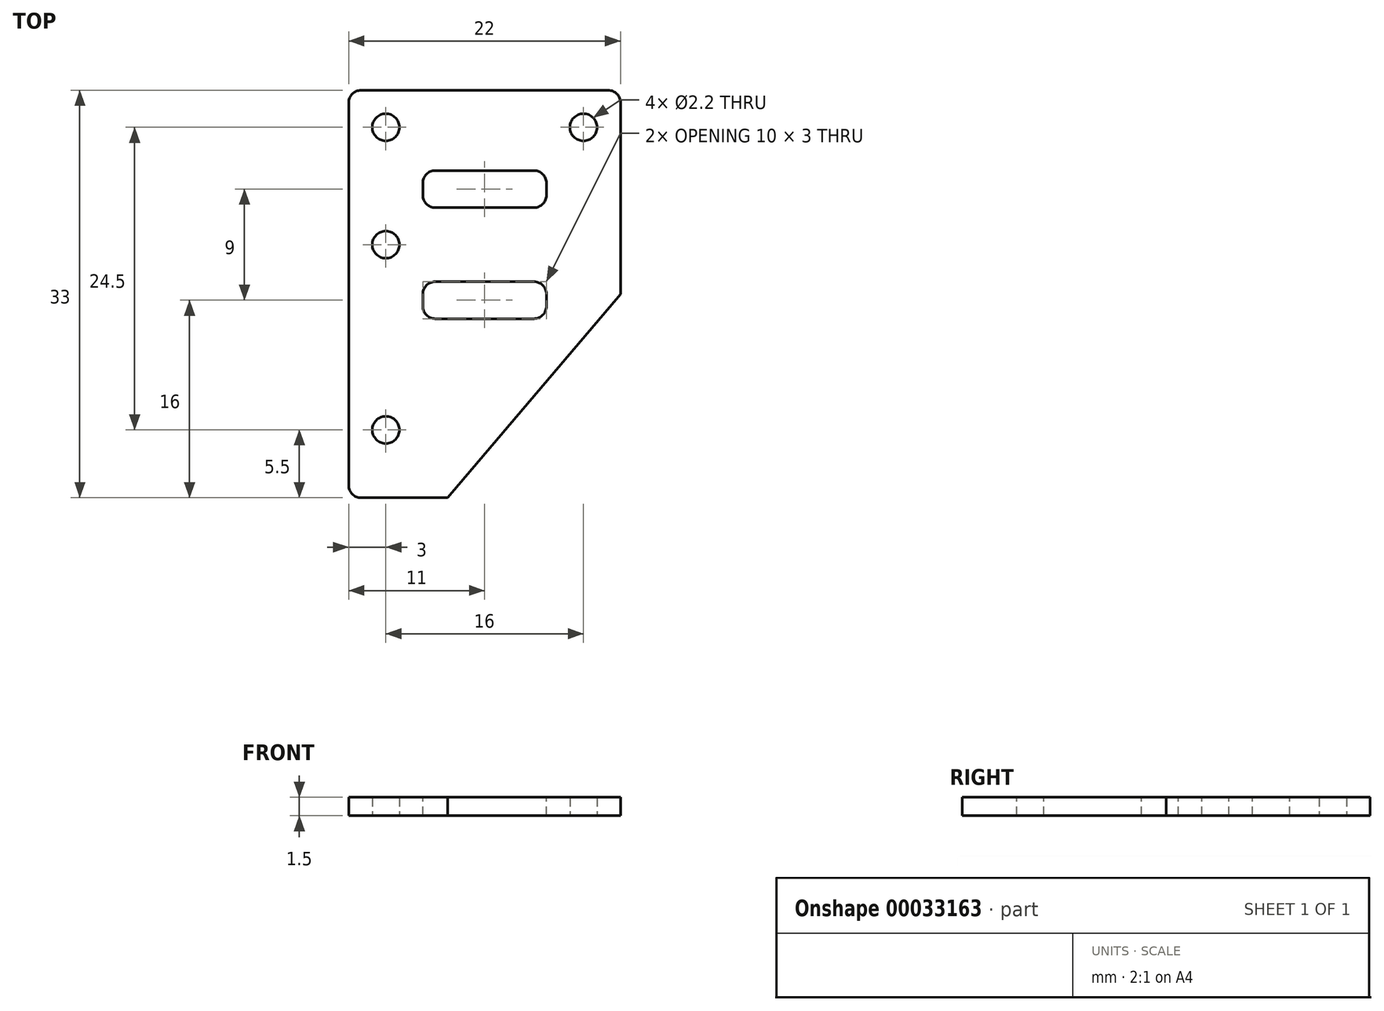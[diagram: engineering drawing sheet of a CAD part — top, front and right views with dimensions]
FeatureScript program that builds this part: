
annotation { "Feature Type Name" : "Feature", "Feature Type Description" : "" }
export const myFeature = defineFeature(function(context is Context, id is Id, definition is map)
    precondition{}
    {
        {
            var Q0;
            Q0=qCreatedBy(makeId("Top.planeOp"),FACE);
            var sketch = newSketch(context, id + "F0", { "sketchPlane" : qUnion([Q0])});
            skLineSegment(sketch, "E0.bottom", {"start": v(11, 16.5) * mm, "end": v(-11, 16.5) * mm});
            skLineSegment(sketch, "E0.top", {"start": v(11, -16.5) * mm, "end": v(-11, -16.5) * mm});
            skLineSegment(sketch, "E0.left", {"start": v(11, 16.5) * mm, "end": v(11, -16.5) * mm});
            skLineSegment(sketch, "E0.right", {"start": v(-11, 16.5) * mm, "end": v(-11, -16.5) * mm});
            skPoint(sketch, "E0.middle", {"position": v(0, 0) * mm});
            skCircle(sketch, "E1", {"center": v(8, 13.5) * mm, "radius": 1.1 * mm});
            skCircle(sketch, "E2.MirrorC", {"center": v(-8, 13.5) * mm, "radius": 1.1 * mm});
            skSolve(sketch);
        }
        {
            var Q0;
            {var subQ4=sQuery(id+"F0.wireOp",EDGE,"E0.bottom");Q0=makeQuery(id+"F0.imprint","IMPRINT",FACE,{"disambiguationData":[TD([[makeQuery(id+"F0.imprint","IMPRINT",EDGE,{"derivedFrom":subQ4}),1.0]])]});}
            var Q1;
            {var subQ2=sQuery(id+"F0.wireOp",EDGE,"f1e16323-2be2-4770-a9bf-99cfb16d4013.1.0.0");Q1=makeQuery(id+"F0.imprint","IMPRINT",FACE,{"disambiguationData":[TD([[makeQuery(id+"F0.imprint","IMPRINT",EDGE,{"derivedFrom":subQ2}),-1.0]])]});}
            extrude(context, id + "F1", {"entities" : qUnion([Q0, Q1]), "depth" : 1.5 * mm});
        }
        {
            var Q0;
            Q0=makeQuery(id+"F1.opExtrude","CAP_FACE",FACE,{"disambiguationData":[OSD([sQuery(id+"F0.wireOp",EDGE,"E0.bottom"),sQuery(id+"F0.wireOp",EDGE,"E0.top"),sQuery(id+"F0.wireOp",EDGE,"E0.left"),sQuery(id+"F0.wireOp",EDGE,"E0.right"),sQuery(id+"F0.wireOp",EDGE,"E1"),sQuery(id+"F0.wireOp",EDGE,"E2.MirrorC"),sQuery(id+"F0.wireOp",EDGE,"1bDBTO5W-hAAF-Dv1a-i1w2-BnnXARTyQX5s"),sQuery(id+"F0.wireOp",EDGE,"f1e16323-2be2-4770-a9bf-99cfb16d4013.1.0.0"),sQuery(id+"F0.wireOp",EDGE,"jiPMqsls-zV3J-hMdb-mDSb-S4SgiakzvMcZ")])],"isStart":false});
            var sketch = newSketch(context, id + "F2", { "sketchPlane" : qUnion([Q0])});
            skLineSegment(sketch, "E3", {"start": v(0, 16.5) * mm, "end": v(0, -16.5) * mm, "construction": true});
            skLineSegment(sketch, "E4.bottom", {"start": v(-4, 10) * mm, "end": v(4, 10) * mm});
            skLineSegment(sketch, "E4.top", {"start": v(-4, 7) * mm, "end": v(4, 7) * mm});
            skLineSegment(sketch, "E4.left", {"start": v(-5, 9) * mm, "end": v(-5, 8) * mm});
            skLineSegment(sketch, "E4.right", {"start": v(5, 9) * mm, "end": v(5, 8) * mm});
            skPoint(sketch, "E4.middle", {"position": v(0, 8.5) * mm});
            skPoint(sketch, "E5", {"position": v(-8, 13.5) * mm});
            skPoint(sketch, "E6.visualSharp", {"position": v(-5, 10) * mm});
            skArc(sketch, "E6.filletArc", {"start": v(-4, 10) * mm, "mid": v(-4.7, 9.7) * mm, "end": v(-5, 9) * mm});
            skPoint(sketch, "E7.visualSharp", {"position": v(-5, 7) * mm});
            skArc(sketch, "E7.filletArc", {"start": v(-5, 8) * mm, "mid": v(-4.7, 7.3) * mm, "end": v(-4, 7) * mm});
            skPoint(sketch, "E8.visualSharp", {"position": v(5, 10) * mm});
            skArc(sketch, "E8.filletArc", {"start": v(5, 9) * mm, "mid": v(4.7, 9.7) * mm, "end": v(4, 10) * mm});
            skPoint(sketch, "E9.visualSharp", {"position": v(5, 7) * mm});
            skArc(sketch, "E9.filletArc", {"start": v(4, 7) * mm, "mid": v(4.7, 7.3) * mm, "end": v(5, 8) * mm});
            skPoint(sketch, "E10.1.0.0", {"position": v(5, 1) * mm});
            skPoint(sketch, "E10.1.0.1", {"position": v(0, -0.5) * mm});
            skPoint(sketch, "E10.1.0.2", {"position": v(-5, 1) * mm});
            skPoint(sketch, "E10.1.0.3", {"position": v(-5, -2) * mm});
            skPoint(sketch, "E10.1.0.4", {"position": v(5, -2) * mm});
            skLineSegment(sketch, "E10.1.0.5", {"start": v(-4, 1) * mm, "end": v(4, 1) * mm});
            skLineSegment(sketch, "E10.1.0.6", {"start": v(-4, -2) * mm, "end": v(4, -2) * mm});
            skArc(sketch, "E10.1.0.7", {"start": v(4, -2) * mm, "mid": v(4.7, -1.7) * mm, "end": v(5, -1) * mm});
            skArc(sketch, "E10.1.0.8", {"start": v(5, 0) * mm, "mid": v(4.7, 0.7) * mm, "end": v(4, 1) * mm});
            skArc(sketch, "E10.1.0.9", {"start": v(-5, -1) * mm, "mid": v(-4.7, -1.7) * mm, "end": v(-4, -2) * mm});
            skLineSegment(sketch, "E10.1.0.10", {"start": v(-5, 0) * mm, "end": v(-5, -1) * mm});
            skLineSegment(sketch, "E10.1.0.11", {"start": v(5, 0) * mm, "end": v(5, -1) * mm});
            skArc(sketch, "E10.1.0.12", {"start": v(-4, 1) * mm, "mid": v(-4.7, 0.7) * mm, "end": v(-5, 0) * mm});
            skLineSegment(sketch, "E10.direction1", {"start": v(-5, 7) * mm, "end": v(-5, -2) * mm, "construction": true});
            skLineSegment(sketch, "E11", {"start": v(11, 0) * mm, "end": v(-3, -16.5) * mm});
            skLineSegment(sketch, "E12", {"start": v(-8, 16.5) * mm, "end": v(-8, -16.5) * mm, "construction": true});
            skCircle(sketch, "E13", {"center": v(-8, 4) * mm, "radius": 1.1 * mm});
            skCircle(sketch, "E14", {"center": v(-8, -11) * mm, "radius": 1.1 * mm});
            skSolve(sketch);
        }
        {
            var Q0;
            {var subQ0=sQuery(id+"F2.wireOp",EDGE,"O1MCrC0z-BeoC-gMcI-JBW4-A8Bq1EHIL6bz");Q0=makeQuery(id+"F2.imprint","IMPRINT",FACE,{"disambiguationData":[TD([[makeQuery(id+"F2.imprint","IMPRINT",EDGE,{"derivedFrom":subQ0}),-1.0]])]});}
            var Q1;
            Q1=makeQuery(id+"F2.imprint","IMPRINT",FACE,{"disambiguationData":[TD([[makeQuery(id+"F2.imprint","IMPRINT",EDGE,{"derivedFrom":sQuery(id+"F2.wireOp",EDGE,"E4.bottom")}),-1.0]])]});
            var Q2;
            Q2=makeQuery(id+"F2.imprint","IMPRINT",FACE,{"disambiguationData":[TD([[makeQuery(id+"F2.imprint","IMPRINT",EDGE,{"derivedFrom":sQuery(id+"F2.wireOp",EDGE,"E10.1.0.5")}),-1.0]])]});
            var Q3;
            {var subQ0=sQuery(id+"F2.wireOp",EDGE,"E11");Q3=makeQuery(id+"F2.imprint","IMPRINT",FACE,{"disambiguationData":[TD([[makeQuery(id+"F2.imprint","IMPRINT",EDGE,{"derivedFrom":subQ0}),1.0]])]});}
            var Q4;
            Q4=makeQuery(id+"F2.imprint","IMPRINT",FACE,{"disambiguationData":[TD([[makeQuery(id+"F2.imprint","IMPRINT",EDGE,{"derivedFrom":sQuery(id+"F2.wireOp",EDGE,"E13")}),1.0]])]});
            var Q5;
            Q5=makeQuery(id+"F2.imprint","IMPRINT",FACE,{"disambiguationData":[TD([[makeQuery(id+"F2.imprint","IMPRINT",EDGE,{"derivedFrom":sQuery(id+"F2.wireOp",EDGE,"E14")}),1.0]])]});
            extrude(context, id + "F3", {"entities" : qUnion([Q0, Q1, Q2, Q3, Q4, Q5]), "operationType" : NewBodyOperationType.REMOVE, "endBound" : BoundingType.UP_TO_NEXT, "oppositeDirection" : true, "depth" : 25 * mm});
        }
        {
            var Q0;
            Q0=makeQuery(id+"F1.opExtrude","SWEPT_EDGE",EDGE,{"disambiguationData":[OSD([sQuery(id+"F0.wireOp",EDGE,"E0.bottom"),sQuery(id+"F0.wireOp",EDGE,"E0.right")])]});
            var Q1;
            Q1=makeQuery(id+"F1.opExtrude","SWEPT_EDGE",EDGE,{"disambiguationData":[OSD([sQuery(id+"F0.wireOp",EDGE,"E0.bottom"),sQuery(id+"F0.wireOp",EDGE,"E0.left")])]});
            var Q2;
            Q2=makeQuery(id+"F1.opExtrude","SWEPT_EDGE",EDGE,{"disambiguationData":[OSD([sQuery(id+"F0.wireOp",EDGE,"E0.top"),sQuery(id+"F0.wireOp",EDGE,"E0.right")])]});
            var Q3;
            Q3=makeQuery(id+"F3.boolean.opBoolean","COPY",EDGE,{"derivedFrom":makeQuery(id+"F3.opExtrude","SWEPT_EDGE",EDGE,{"disambiguationData":[OSD([sQuery(id+"F0.wireOp",EDGE,"E0.left"),sQuery(id+"F2.wireOp",EDGE,"E11")])]})});
            var Q4;
            Q4=makeQuery(id+"F3.boolean.opBoolean","COPY",EDGE,{"derivedFrom":makeQuery(id+"F3.opExtrude","SWEPT_EDGE",EDGE,{"disambiguationData":[OSD([sQuery(id+"F0.wireOp",EDGE,"E0.top"),sQuery(id+"F2.wireOp",EDGE,"E11")])]})});
            fillet(context, id + "F4", {"entities" : qUnion([Q0, Q1, Q2, Q3, Q4]), "radius" : 1 * mm, "tangentPropagation" : true, "allowEdgeOverflow" : false});
        }
    });
